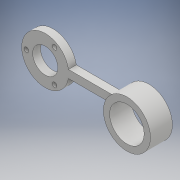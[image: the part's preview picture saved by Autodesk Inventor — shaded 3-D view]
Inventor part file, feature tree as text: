
AUTODESK INVENTOR PART (.ipt)
format: ipt  version: 2017 SP1 (Build 210196100, 196)  size: 270,336 bytes
history: native  units: mm
features: sketch x4, extrude x3, hole x1
ambient origin geometry x8: Origin, YZ Plane, XZ Plane, XY Plane, X Axis, Y Axis, Z Axis, Center Point
bodies: Solide1 (feature_tree)
feature tree (8):
  extrude  "Extrusion1"  Depth=30.0mm
  hole  "Perçage1"  [1 undecoded]
  extrude  "Extrusion2"  Depth=5.0mm TaperAngle=0.0deg
  extrude  "Extrusion3"  Depth=12.0mm
  sketch  "Esquisse1"
  sketch  "Esquisse2"
  sketch  "Esquisse3"
  sketch  "Esquisse4"
note: 1 required parameter value undecoded (feature->parameter linkage not recoverable at this tier; creation-order binding heuristic only, values carry confidence <= 0.55)
